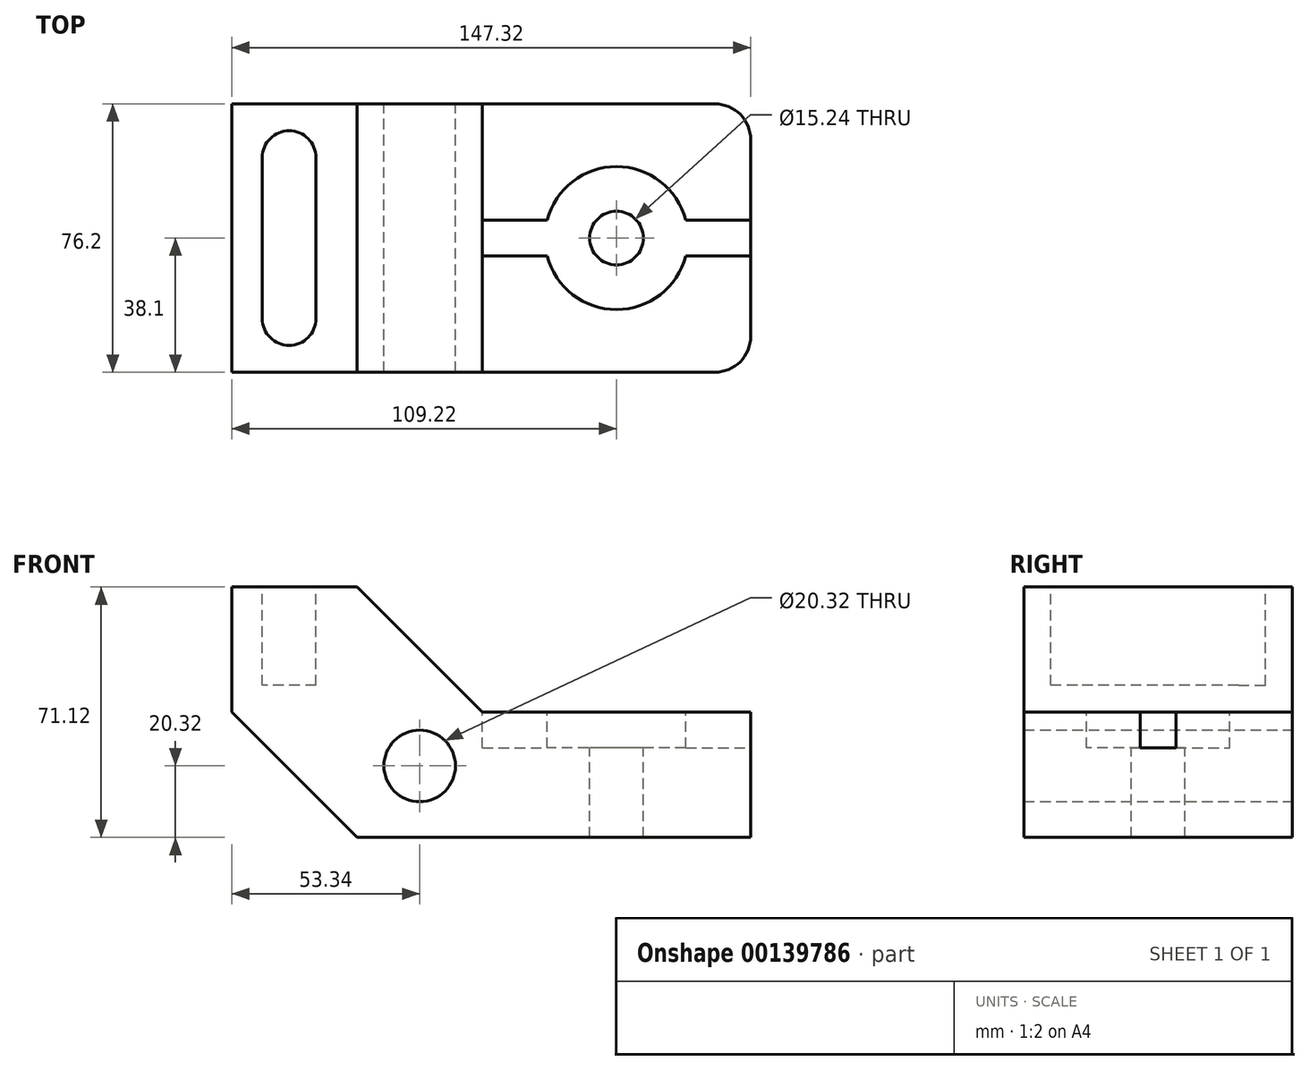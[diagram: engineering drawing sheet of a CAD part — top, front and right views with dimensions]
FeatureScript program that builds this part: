
annotation { "Feature Type Name" : "Feature", "Feature Type Description" : "" }
export const myFeature = defineFeature(function(context is Context, id is Id, definition is map)
    precondition{}
    {
        {
            var Q0;
            Q0=qCreatedBy(makeId("Front.planeOp"),FACE);
            var sketch = newSketch(context, id + "F0", { "sketchPlane" : qUnion([Q0])});
            skLineSegment(sketch, "E0", {"start": v(0, 71.12) * mm, "end": v(0, 35.56) * mm});
            skLineSegment(sketch, "E1", {"start": v(0, 35.56) * mm, "end": v(35.56, 0) * mm});
            skLineSegment(sketch, "E2", {"start": v(35.56, 0) * mm, "end": v(147.32, 0) * mm});
            skLineSegment(sketch, "E3", {"start": v(147.32, 0) * mm, "end": v(147.32, 35.56) * mm});
            skLineSegment(sketch, "E4", {"start": v(147.32, 35.56) * mm, "end": v(71.12, 35.56) * mm});
            skLineSegment(sketch, "E5", {"start": v(71.12, 35.56) * mm, "end": v(35.56, 71.12) * mm});
            skLineSegment(sketch, "E6", {"start": v(35.56, 71.12) * mm, "end": v(0, 71.12) * mm});
            skSolve(sketch);
        }
        {
            var Q0;
            Q0 = qSketchRegion(id + "F0", true);
            extrude(context, id + "F1", {"entities" : qUnion([Q0]), "depth" : 76.2 * mm});
        }
        {
            var Q0;
            Q0=makeQuery(id+"F1.opExtrude","SWEPT_FACE",FACE,{"disambiguationData":[OSD([sQuery(id+"F0.wireOp",EDGE,"E6")])]});
            cPlane(context, id + "F2", {"entities" : qUnion([Q0]), "cplaneType" : CPlaneType.OFFSET, "offset" : 0 * mm, "width" : 152.4 * mm, "height" : 152.4 * mm});
        }
        {
            var Q0;
            Q0=qCreatedBy(id+"F2.planeOp",FACE);
            var sketch = newSketch(context, id + "F3", { "sketchPlane" : qUnion([Q0])});
            skLineSegment(sketch, "E7", {"start": v(16.27, -15.24) * mm, "end": v(16.27, -60.96) * mm, "construction": true});
            skArc(sketch, "E8.0.startCap", {"start": v(8.65, -15.24) * mm, "mid": v(16.27, -7.62) * mm, "end": v(23.9, -15.24) * mm});
            skArc(sketch, "E8.0.endCap", {"start": v(23.9, -60.96) * mm, "mid": v(16.27, -68.58) * mm, "end": v(8.65, -60.96) * mm});
            skLineSegment(sketch, "E8.0.left", {"start": v(23.9, -15.24) * mm, "end": v(23.9, -60.96) * mm});
            skLineSegment(sketch, "E8.0.right", {"start": v(8.65, -15.24) * mm, "end": v(8.65, -60.96) * mm});
            skSolve(sketch);
        }
        {
            var Q0;
            Q0 = qSketchRegion(id + "F3", true);
            extrude(context, id + "F4", {"entities" : qUnion([Q0]), "operationType" : NewBodyOperationType.REMOVE, "oppositeDirection" : true, "depth" : 27.94 * mm});
        }
        {
            var Q0;
            Q0=qCreatedBy(makeId("Front.planeOp"),FACE);
            var sketch = newSketch(context, id + "F5", { "sketchPlane" : qUnion([Q0])});
            skCircle(sketch, "E9", {"center": v(53.34, 20.32) * mm, "radius": 10.16 * mm});
            skSolve(sketch);
        }
        {
            var Q0;
            Q0 = qSketchRegion(id + "F5", true);
            extrude(context, id + "F6", {"entities" : qUnion([Q0]), "operationType" : NewBodyOperationType.REMOVE, "endBound" : BoundingType.THROUGH_ALL, "depth" : 25.4 * mm});
        }
        {
            var Q0;
            Q0=makeQuery(id+"F1.opExtrude","SWEPT_FACE",FACE,{"disambiguationData":[OSD([sQuery(id+"F0.wireOp",EDGE,"E4")])]});
            var sketch = newSketch(context, id + "F7", { "sketchPlane" : qUnion([Q0])});
            skPoint(sketch, "E10", {"position": v(109.22, -38.1) * mm});
            skSolve(sketch);
        }
        {
            var Q0;
            Q0=sQuery(id+"F7.wireOp",VERTEX,"E10");
            var Q1;
            Q1=makeQuery(id+"F1.opExtrude","SWEPT_BODY",BODY,{"disambiguationData":[OSD([sQuery(id+"F0.wireOp",EDGE,"E0"),sQuery(id+"F0.wireOp",EDGE,"E1"),sQuery(id+"F0.wireOp",EDGE,"E2"),sQuery(id+"F0.wireOp",EDGE,"E3"),sQuery(id+"F0.wireOp",EDGE,"E4"),sQuery(id+"F0.wireOp",EDGE,"E5"),sQuery(id+"F0.wireOp",EDGE,"E6")])]});
            hole(context, id + "F8", {"style" : HoleStyle.C_BORE, "endStyle" : HoleEndStyle.THROUGH, "holeDiameter" : 15.24 * mm, "cBoreDiameter" : 40.64 * mm, "cBoreDepth" : 10.16 * mm, "locations" : qUnion([Q0]), "scope" : qUnion([Q1]), "isTappedThrough" : true});
        }
        {
            var Q0;
            Q0=makeQuery(id+"F1.opExtrude","SWEPT_FACE",FACE,{"disambiguationData":[OSD([sQuery(id+"F0.wireOp",EDGE,"E4")])]});
            cPlane(context, id + "F9", {"entities" : qUnion([Q0]), "cplaneType" : CPlaneType.OFFSET, "offset" : 0 * mm, "width" : 152.4 * mm, "height" : 152.4 * mm});
        }
        {
            var Q0;
            Q0=qCreatedBy(id+"F9.planeOp",FACE);
            var sketch = newSketch(context, id + "F10", { "sketchPlane" : qUnion([Q0])});
            skLineSegment(sketch, "E11", {"start": v(128.9, -33.02) * mm, "end": v(147.32, -33.02) * mm});
            skLineSegment(sketch, "E12", {"start": v(147.32, -33.02) * mm, "end": v(147.32, -38.1) * mm});
            skLineSegment(sketch, "E13", {"start": v(147.32, -38.1) * mm, "end": v(129.54, -38.1) * mm, "construction": true});
            skLineSegment(sketch, "E14", {"start": v(71.12, -33.02) * mm, "end": v(89.55, -33.02) * mm});
            skLineSegment(sketch, "E15", {"start": v(71.12, -43.18) * mm, "end": v(89.55, -43.18) * mm});
            skLineSegment(sketch, "E16", {"start": v(71.12, -33.02) * mm, "end": v(71.12, -43.18) * mm});
            skLineSegment(sketch, "E17", {"start": v(128.9, -43.18) * mm, "end": v(147.32, -43.18) * mm});
            skLineSegment(sketch, "E18", {"start": v(147.32, -43.18) * mm, "end": v(147.32, -38.1) * mm});
            skArc(sketch, "E19", {"start": v(89.55, -33.02) * mm, "mid": v(88.9, -38.1) * mm, "end": v(89.55, -43.18) * mm});
            skArc(sketch, "E20", {"start": v(128.9, -33.02) * mm, "mid": v(129.54, -38.1) * mm, "end": v(128.9, -43.18) * mm});
            skSolve(sketch);
        }
        {
            var Q0;
            Q0 = qSketchRegion(id + "F10", true);
            extrude(context, id + "F11", {"entities" : qUnion([Q0]), "operationType" : NewBodyOperationType.REMOVE, "oppositeDirection" : true, "depth" : 10.16 * mm});
        }
        {
            var Q0;
            Q0=makeQuery(id+"F1.opExtrude","CAP_EDGE",EDGE,{"disambiguationData":[OSD([sQuery(id+"F0.wireOp",EDGE,"E3")])],"isStart":true});
            var Q1;
            Q1=makeQuery(id+"F1.opExtrude","CAP_EDGE",EDGE,{"disambiguationData":[OSD([sQuery(id+"F0.wireOp",EDGE,"E3")])],"isStart":false});
            fillet(context, id + "F12", {"entities" : qUnion([Q0, Q1]), "radius" : 10.16 * mm, "tangentPropagation" : true, "allowEdgeOverflow" : false});
        }
    });
